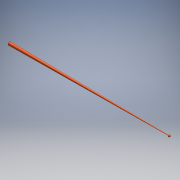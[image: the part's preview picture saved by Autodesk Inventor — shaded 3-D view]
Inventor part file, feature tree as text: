
AUTODESK INVENTOR PART (.ipt)
format: ipt  version: 2016 (Build 200138000, 138)  size: 103,936 bytes
history: native  units: mm
features: sketch x3, plane x1, loft x1, revolve x1
ambient origin geometry x8: Origin, YZ Plane, XZ Plane, XY Plane, X Axis, Y Axis, Z Axis, Center Point
bodies: Solid1 (feature_tree)
feature tree (6):
  sketch  "Sketch1"  dims[d0=30.0mm d1=1500.0mm]
  plane  "Work Plane1"
  loft  "Loft1"
  revolve  "Revolution1"  Angle=90.0deg
  sketch  "Sketch2"  dims[d2=5.0mm d3=0.0mm d4=90.0deg]
  sketch  "Sketch3"  dims[d5=0.0mm d6=90.0deg d7=20.0mm d8=0.0mm d9=90.0deg]
